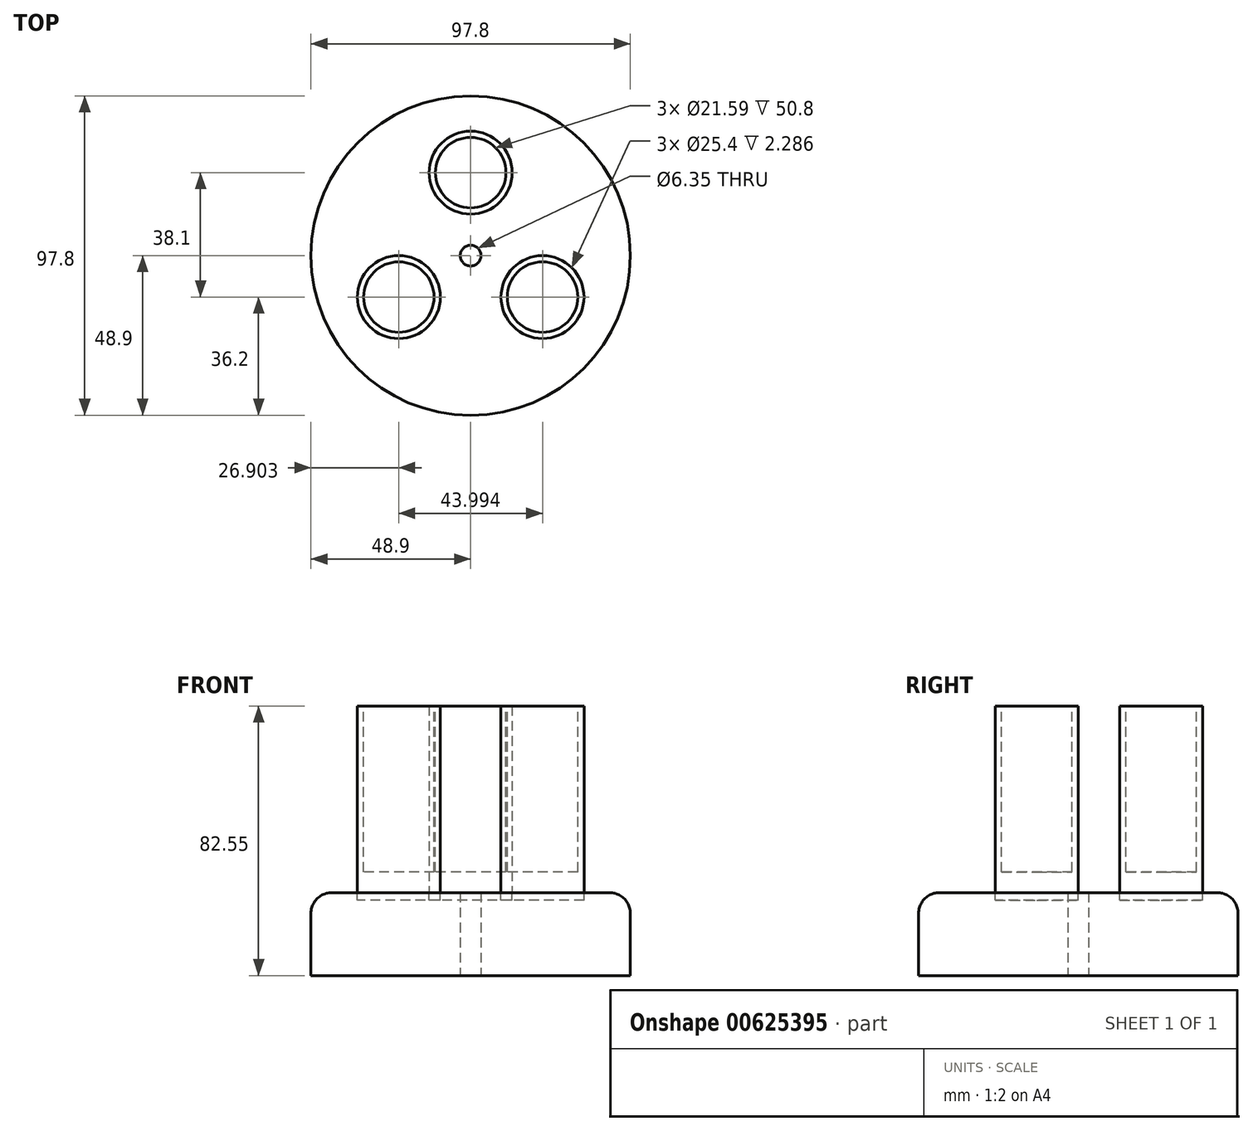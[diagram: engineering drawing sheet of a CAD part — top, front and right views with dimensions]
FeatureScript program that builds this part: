
annotation { "Feature Type Name" : "Feature", "Feature Type Description" : "" }
export const myFeature = defineFeature(function(context is Context, id is Id, definition is map)
    precondition{}
    {
        {
            var Q0;
            Q0=qCreatedBy(makeId("Top.planeOp"),FACE);
            var sketch = newSketch(context, id + "F0", { "sketchPlane" : qUnion([Q0])});
            skCircle(sketch, "E0", {"center": v(0, 0) * mm, "radius": 48.9 * mm});
            skCircle(sketch, "E1", {"center": v(0, 0) * mm, "radius": 3.18 * mm});
            skSolve(sketch);
        }
        {
            var Q0;
            Q0=makeQuery(id+"F0.imprint","IMPRINT",FACE,{"disambiguationData":[TD([[makeQuery(id+"F0.imprint","IMPRINT",EDGE,{"derivedFrom":sQuery(id+"F0.wireOp",EDGE,"E0")}),1.0]])]});
            extrude(context, id + "F1", {"entities" : qUnion([Q0]), "depth" : 25.4 * mm, "offsetDistance" : 25.4 * mm});
        }
        {
            var Q0;
            Q0=makeQuery(id+"F1.opExtrude","CAP_EDGE",EDGE,{"disambiguationData":[OSD([sQuery(id+"F0.wireOp",EDGE,"E0")])],"isStart":false});
            fillet(context, id + "F2", {"entities" : qUnion([Q0]), "radius" : 6.35 * mm, "tangentPropagation" : true, "allowEdgeOverflow" : false});
        }
        {
            var Q0;
            Q0=makeQuery(id+"F1.opExtrude","CAP_FACE",FACE,{"disambiguationData":[OSD([sQuery(id+"F0.wireOp",EDGE,"E0"),sQuery(id+"F0.wireOp",EDGE,"E1")])],"isStart":false});
            var sketch = newSketch(context, id + "F3", { "sketchPlane" : qUnion([Q0])});
            skCircle(sketch, "E2", {"center": v(0, 25.4) * mm, "radius": 12.7 * mm});
            skLineSegment(sketch, "E3", {"start": v(-148, 0) * mm, "end": v(173.13, 0) * mm, "construction": true});
            skCircle(sketch, "E4.1.0", {"center": v(-22, -12.7) * mm, "radius": 12.7 * mm});
            skCircle(sketch, "E4.2.0", {"center": v(22, -12.7) * mm, "radius": 12.7 * mm});
            skPoint(sketch, "E4.center", {"position": v(0, 0) * mm});
            skSolve(sketch);
        }
        {
            var Q0;
            Q0=makeQuery(id+"F3.imprint","IMPRINT",FACE,{"disambiguationData":[TD([[makeQuery(id+"F3.imprint","IMPRINT",EDGE,{"derivedFrom":sQuery(id+"F3.wireOp",EDGE,"E2")}),1.0]])]});
            var Q1;
            Q1=makeQuery(id+"F3.imprint","IMPRINT",FACE,{"disambiguationData":[TD([[makeQuery(id+"F3.imprint","IMPRINT",EDGE,{"derivedFrom":sQuery(id+"F3.wireOp",EDGE,"E4.1.0")}),1.0]])]});
            var Q2;
            Q2=makeQuery(id+"F3.imprint","IMPRINT",FACE,{"disambiguationData":[TD([[makeQuery(id+"F3.imprint","IMPRINT",EDGE,{"derivedFrom":sQuery(id+"F3.wireOp",EDGE,"E4.2.0")}),1.0]])]});
            extrude(context, id + "F4", {"entities" : qUnion([Q0, Q1, Q2]), "operationType" : NewBodyOperationType.ADD, "depth" : 57.15 * mm, "offsetDistance" : 25.4 * mm});
        }
        {
            var Q0;
            Q0=makeQuery(id+"F4.opExtrude","CAP_FACE",FACE,{"disambiguationData":[OSD([sQuery(id+"F3.wireOp",EDGE,"E4.2.0")])],"isStart":false});
            var sketch = newSketch(context, id + "F5", { "sketchPlane" : qUnion([Q0])});
            skCircle(sketch, "E5", {"center": v(22, -12.7) * mm, "radius": 10.8 * mm});
            skSolve(sketch);
        }
        {
            var Q0;
            Q0=makeQuery(id+"F5.imprint","IMPRINT",FACE,{"disambiguationData":[TD([[makeQuery(id+"F5.imprint","IMPRINT",EDGE,{"derivedFrom":sQuery(id+"F5.wireOp",EDGE,"E5")}),1.0]])]});
            extrude(context, id + "F6", {"entities" : qUnion([Q0]), "operationType" : NewBodyOperationType.REMOVE, "oppositeDirection" : true, "depth" : 50.8 * mm, "offsetDistance" : 25.4 * mm});
        }
        {
            var Q0;
            Q0=makeQuery(id+"F4.opExtrude","CAP_FACE",FACE,{"disambiguationData":[OSD([sQuery(id+"F3.wireOp",EDGE,"E4.1.0")])],"isStart":false});
            var sketch = newSketch(context, id + "F7", { "sketchPlane" : qUnion([Q0])});
            skCircle(sketch, "E6", {"center": v(-22, -12.7) * mm, "radius": 10.8 * mm});
            skSolve(sketch);
        }
        {
            var Q0;
            Q0=makeQuery(id+"F7.imprint","IMPRINT",FACE,{"disambiguationData":[TD([[makeQuery(id+"F7.imprint","IMPRINT",EDGE,{"derivedFrom":sQuery(id+"F7.wireOp",EDGE,"E6")}),1.0]])]});
            extrude(context, id + "F8", {"entities" : qUnion([Q0]), "operationType" : NewBodyOperationType.REMOVE, "oppositeDirection" : true, "depth" : 50.8 * mm, "offsetDistance" : 25.4 * mm});
        }
        {
            var Q0;
            Q0=makeQuery(id+"F4.opExtrude","CAP_FACE",FACE,{"disambiguationData":[OSD([sQuery(id+"F3.wireOp",EDGE,"E2")])],"isStart":false});
            var sketch = newSketch(context, id + "F9", { "sketchPlane" : qUnion([Q0])});
            skCircle(sketch, "E7", {"center": v(0, 25.4) * mm, "radius": 10.8 * mm});
            skSolve(sketch);
        }
        {
            var Q0;
            Q0=makeQuery(id+"F9.imprint","IMPRINT",FACE,{"disambiguationData":[TD([[makeQuery(id+"F9.imprint","IMPRINT",EDGE,{"derivedFrom":sQuery(id+"F9.wireOp",EDGE,"E7")}),1.0]])]});
            extrude(context, id + "F10", {"entities" : qUnion([Q0]), "operationType" : NewBodyOperationType.REMOVE, "oppositeDirection" : true, "depth" : 50.8 * mm, "offsetDistance" : 25.4 * mm});
        }
        {
            var Q0;
            Q0 = qSketchRegion(id + "F3", true);
            extrude(context, id + "F11", {"entities" : qUnion([Q0]), "operationType" : NewBodyOperationType.REMOVE, "oppositeDirection" : true, "depth" : 2.3 * mm, "offsetDistance" : 25.4 * mm});
        }
    });
